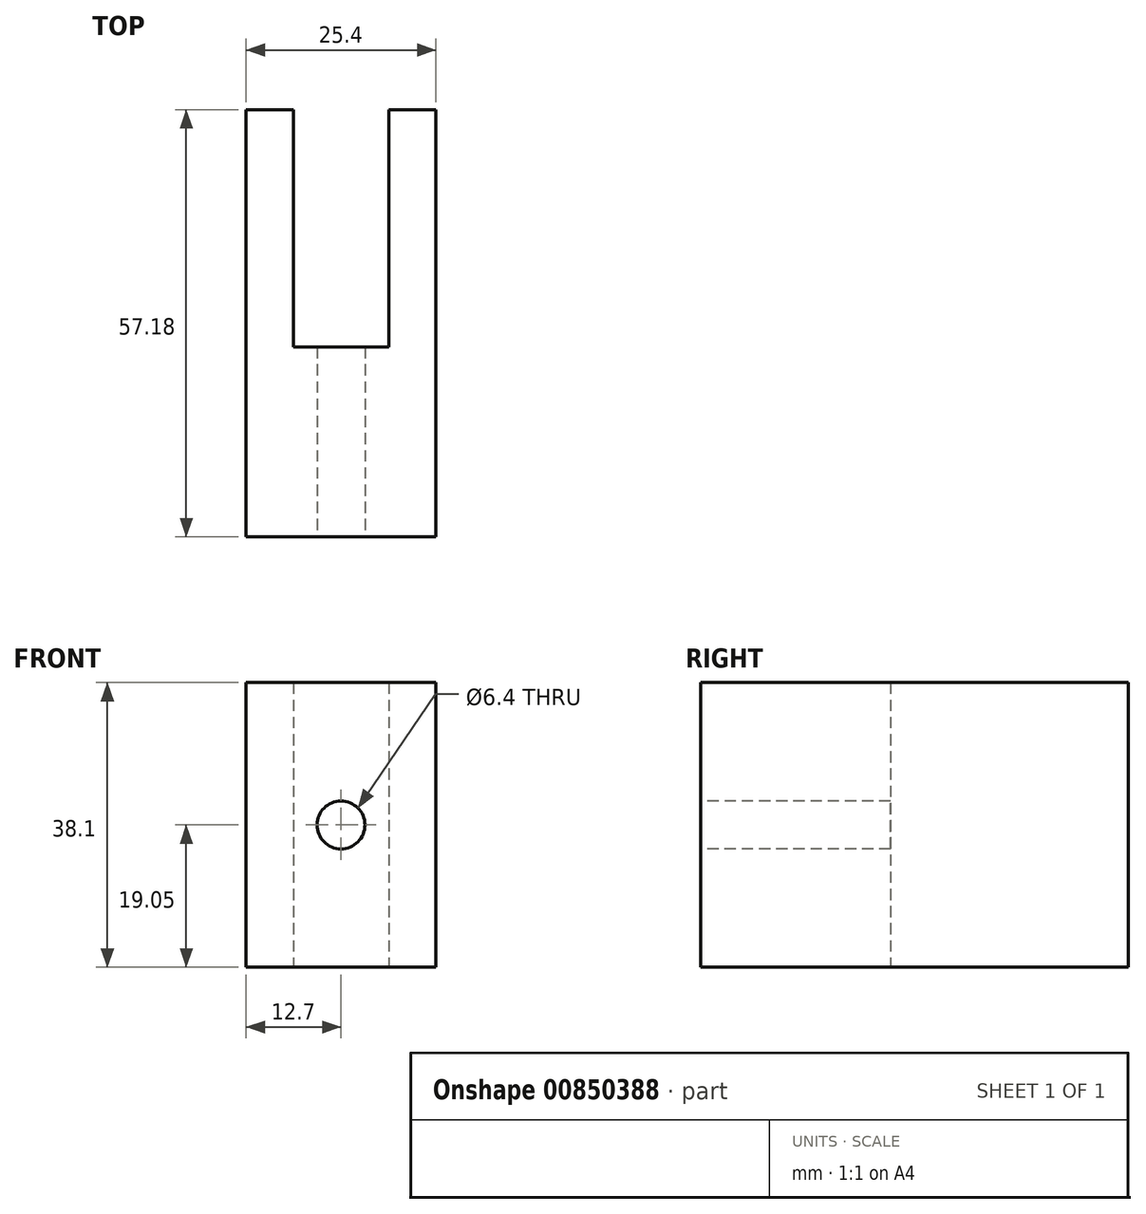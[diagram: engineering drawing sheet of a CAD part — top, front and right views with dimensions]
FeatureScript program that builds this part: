
annotation { "Feature Type Name" : "Feature", "Feature Type Description" : "" }
export const myFeature = defineFeature(function(context is Context, id is Id, definition is map)
    precondition{}
    {
        {
            var Q0;
            Q0=qCreatedBy(makeId("Top.planeOp"),FACE);
            var sketch = newSketch(context, id + "F0", { "sketchPlane" : qUnion([Q0])});
            skLineSegment(sketch, "E0.bottom", {"start": v(12.7, -19.05) * mm, "end": v(-12.7, -19.05) * mm});
            skLineSegment(sketch, "E0.top", {"start": v(12.7, 19.05) * mm, "end": v(-12.7, 19.05) * mm});
            skLineSegment(sketch, "E0.left", {"start": v(12.7, -19.05) * mm, "end": v(12.7, 19.05) * mm});
            skLineSegment(sketch, "E0.right", {"start": v(-12.7, -19.05) * mm, "end": v(-12.7, 19.05) * mm});
            skPoint(sketch, "E0.middle", {"position": v(0, 0) * mm});
            skSolve(sketch);
        }
        {
            var Q0;
            Q0=makeQuery(id+"F0.imprint","IMPRINT",FACE,{"disambiguationData":[TD([[makeQuery(id+"F0.imprint","IMPRINT",EDGE,{"derivedFrom":sQuery(id+"F0.wireOp",EDGE,"E0.bottom")}),-1.0]])]});
            extrude(context, id + "F1", {"entities" : qUnion([Q0]), "endBound" : BoundingType.SYMMETRIC, "depth" : 38.1 * mm, "offsetDistance" : 25 * mm});
        }
        {
            var Q0;
            Q0=makeQuery(id+"F1.opExtrude","SWEPT_FACE",FACE,{"disambiguationData":[OSD([sQuery(id+"F0.wireOp",EDGE,"E0.top")])]});
            var Q1;
            Q1=makeQuery(id+"F1.opExtrude","CAP_FACE",FACE,{"disambiguationData":[OSD([sQuery(id+"F0.wireOp",EDGE,"E0.bottom"),sQuery(id+"F0.wireOp",EDGE,"E0.top"),sQuery(id+"F0.wireOp",EDGE,"E0.left"),sQuery(id+"F0.wireOp",EDGE,"E0.right")])],"isStart":false});
            var Q2;
            Q2=makeQuery(id+"F1.opExtrude","CAP_FACE",FACE,{"disambiguationData":[OSD([sQuery(id+"F0.wireOp",EDGE,"E0.bottom"),sQuery(id+"F0.wireOp",EDGE,"E0.top"),sQuery(id+"F0.wireOp",EDGE,"E0.left"),sQuery(id+"F0.wireOp",EDGE,"E0.right")])],"isStart":true});
            shell(context, id + "F2", {"entities" : qUnion([Q0, Q1, Q2]), "thickness" : 6.33 * mm});
        }
        {
            var Q0;
            Q0=makeQuery(id+"F1.opExtrude","SWEPT_FACE",FACE,{"disambiguationData":[OSD([sQuery(id+"F0.wireOp",EDGE,"E0.bottom")])]});
            extrude(context, id + "F3", {"entities" : qUnion([Q0]), "operationType" : NewBodyOperationType.ADD, "depth" : 19.07 * mm, "offsetDistance" : 25 * mm});
        }
        {
            var Q0;
            Q0=makeQuery(id+"F3.opExtrude","CAP_FACE",FACE,{"disambiguationData":[OSD([sQuery(id+"F0.wireOp",EDGE,"E0.bottom")])],"isStart":false});
            var sketch = newSketch(context, id + "F4", { "sketchPlane" : qUnion([Q0])});
            skPoint(sketch, "E1", {"position": v(0, 0) * mm});
            skSolve(sketch);
        }
        {
            var Q0;
            Q0=sQuery(id+"F4.wireOp",VERTEX,"E1");
            var Q1;
            Q1=makeQuery(id+"F1.opExtrude","SWEPT_BODY",BODY,{"disambiguationData":[OSD([sQuery(id+"F0.wireOp",EDGE,"E0.bottom"),sQuery(id+"F0.wireOp",EDGE,"E0.top"),sQuery(id+"F0.wireOp",EDGE,"E0.left"),sQuery(id+"F0.wireOp",EDGE,"E0.right")])]});
            hole(context, id + "F5", {"style" : HoleStyle.SIMPLE, "endStyle" : HoleEndStyle.BLIND, "holeDiameter" : 6.4 * mm, "majorDiameter" : 5 * mm, "holeDepth" : 50 * mm, "isTappedThrough" : true, "tappedDepth" : 12 * mm, "tapClearance" : 3, "locations" : qUnion([Q0]), "scope" : qUnion([Q1])});
        }
    });
